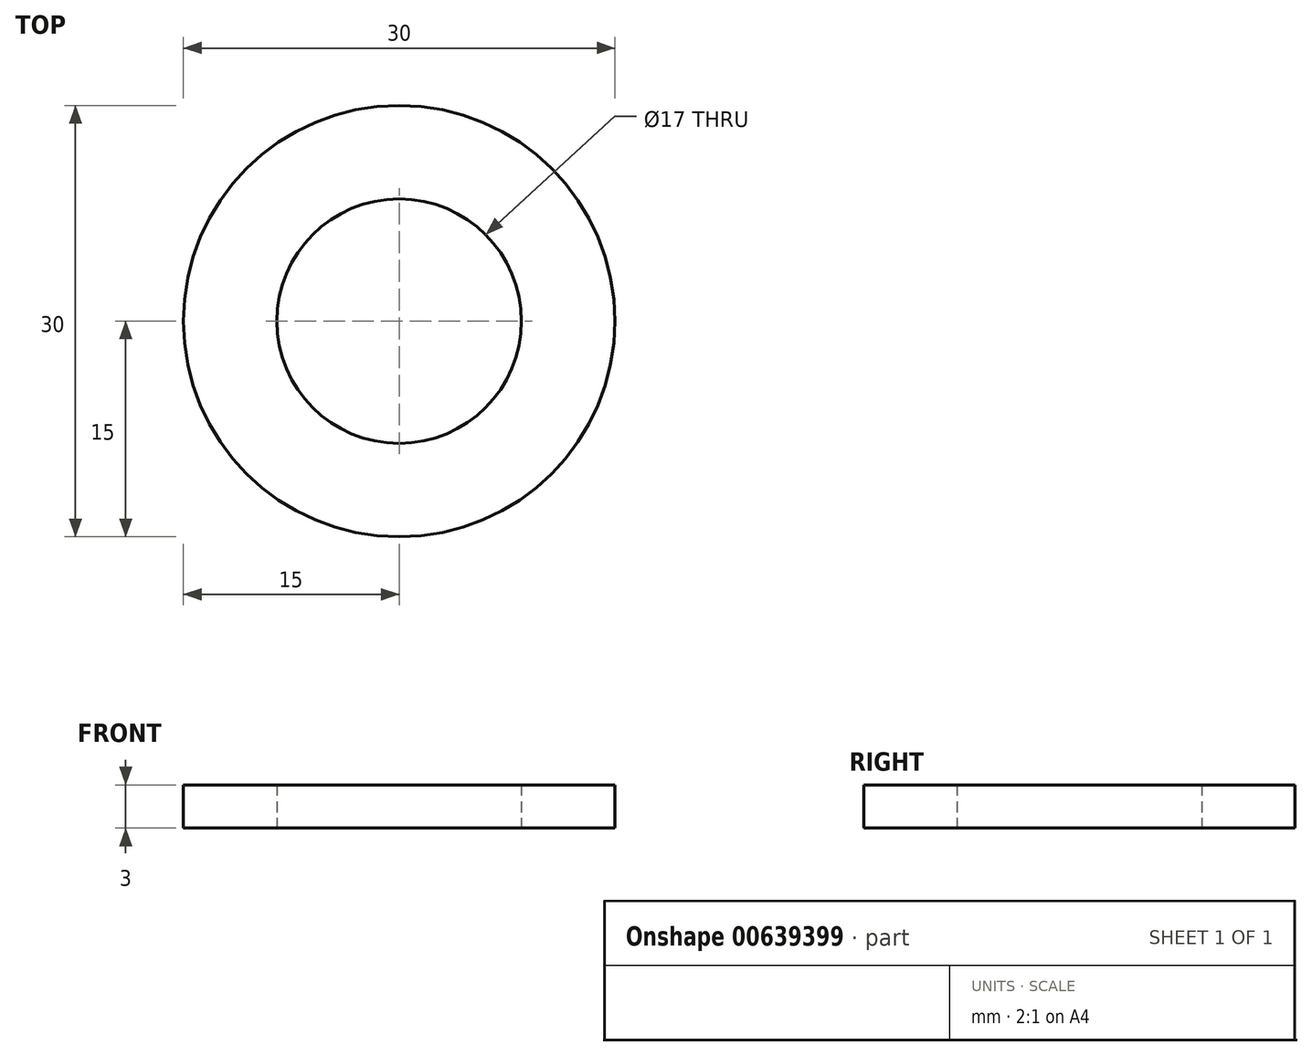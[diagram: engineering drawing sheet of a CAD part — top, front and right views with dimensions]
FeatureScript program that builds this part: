
annotation { "Feature Type Name" : "Feature", "Feature Type Description" : "" }
export const myFeature = defineFeature(function(context is Context, id is Id, definition is map)
    precondition{}
    {
        {
            var Q0;
            Q0=qCreatedBy(makeId("Top.planeOp"),FACE);
            var sketch = newSketch(context, id + "F0", { "sketchPlane" : qUnion([Q0])});
            skCircle(sketch, "E0", {"center": v(0, 0) * mm, "radius": 8.5 * mm});
            skCircle(sketch, "E1", {"center": v(0, 0) * mm, "radius": 15 * mm});
            skSolve(sketch);
        }
        {
            var Q0;
            Q0=makeQuery(id+"F0.imprint","IMPRINT",FACE,{"disambiguationData":[TD([[makeQuery(id+"F0.imprint","IMPRINT",EDGE,{"derivedFrom":sQuery(id+"F0.wireOp",EDGE,"E0")}),-1.0]])]});
            extrude(context, id + "F1", {"entities" : qUnion([Q0]), "depth" : 3 * mm, "offsetDistance" : 25 * mm});
        }
    });
